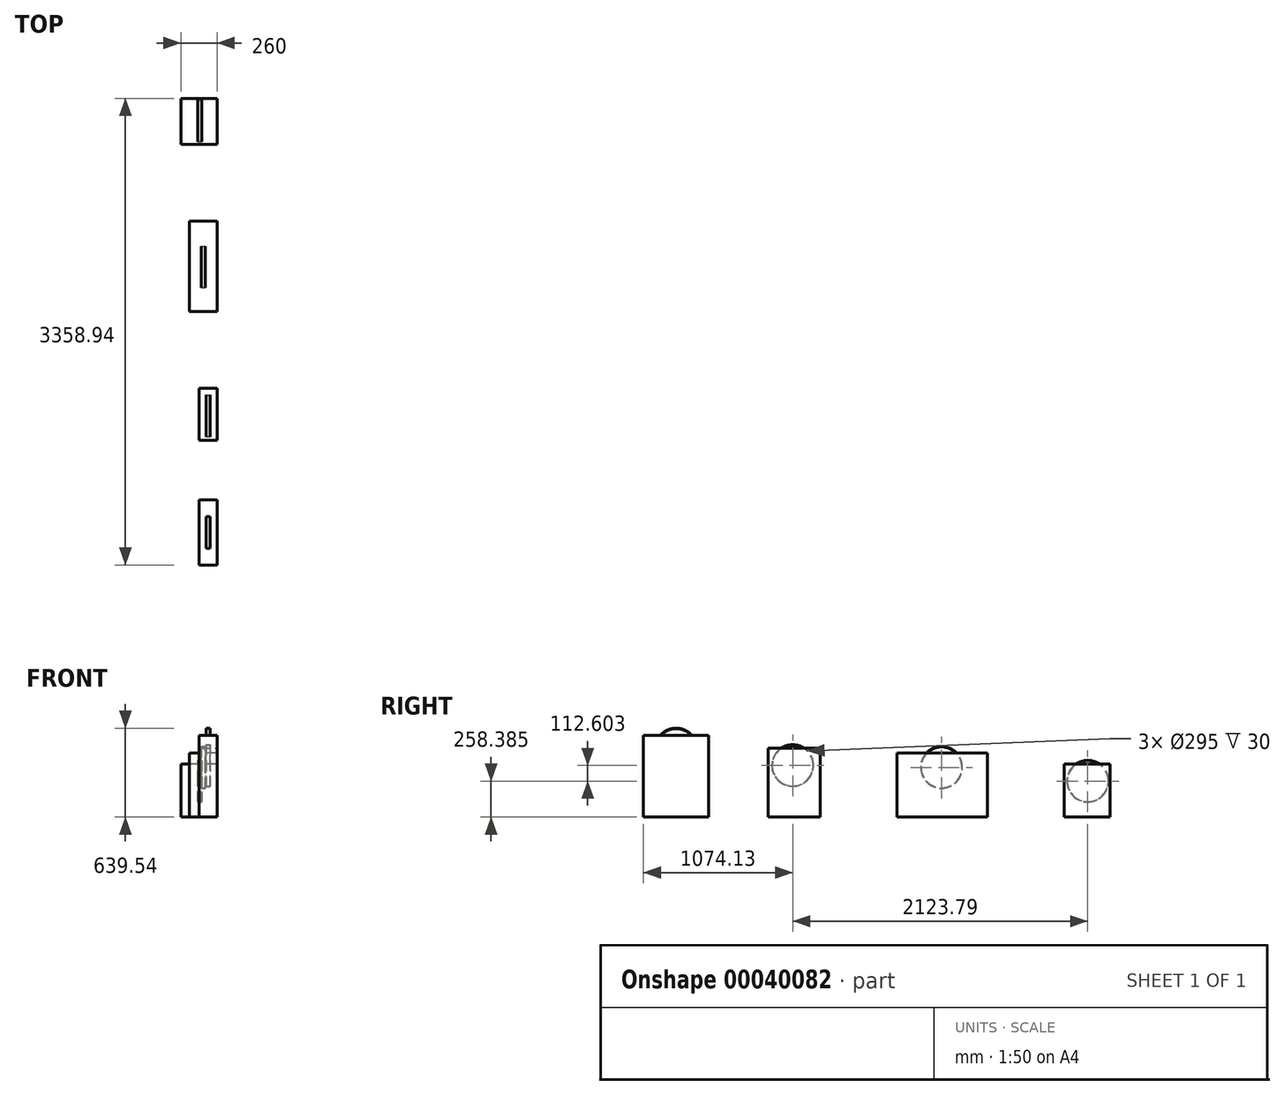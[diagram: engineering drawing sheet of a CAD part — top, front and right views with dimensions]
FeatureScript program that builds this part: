
annotation { "Feature Type Name" : "Feature", "Feature Type Description" : "" }
export const myFeature = defineFeature(function(context is Context, id is Id, definition is map)
    precondition{}
    {
        {
            var Q0;
            Q0=qCreatedBy(makeId("Top.planeOp"),FACE);
            var sketch = newSketch(context, id + "F0", { "sketchPlane" : qUnion([Q0])});
            skLineSegment(sketch, "E0.bottom", {"start": v(-266.62, 237.52) * mm, "end": v(-136.62, 237.52) * mm});
            skLineSegment(sketch, "E0.top", {"start": v(-266.62, -232.48) * mm, "end": v(-136.62, -232.48) * mm});
            skLineSegment(sketch, "E0.left", {"start": v(-266.62, 237.52) * mm, "end": v(-266.62, -232.48) * mm});
            skLineSegment(sketch, "E0.right", {"start": v(-136.62, 237.52) * mm, "end": v(-136.62, -232.48) * mm});
            skLineSegment(sketch, "E1.bottom", {"start": v(-266.62, 664.12) * mm, "end": v(-136.62, 664.12) * mm});
            skLineSegment(sketch, "E1.top", {"start": v(-266.62, 1039.12) * mm, "end": v(-136.62, 1039.12) * mm});
            skLineSegment(sketch, "E1.left", {"start": v(-266.62, 664.12) * mm, "end": v(-266.62, 1039.12) * mm});
            skLineSegment(sketch, "E1.right", {"start": v(-136.62, 664.12) * mm, "end": v(-136.62, 1039.12) * mm});
            skLineSegment(sketch, "E2", {"start": v(-136.62, 237.52) * mm, "end": v(-136.62, 791.19) * mm, "construction": true});
            skLineSegment(sketch, "E3.bottom", {"start": v(-136.62, 1592.79) * mm, "end": v(-336.62, 1592.79) * mm});
            skLineSegment(sketch, "E3.top", {"start": v(-136.62, 2242.79) * mm, "end": v(-336.62, 2242.79) * mm});
            skLineSegment(sketch, "E3.left", {"start": v(-136.62, 1592.79) * mm, "end": v(-136.62, 2242.79) * mm});
            skLineSegment(sketch, "E3.right", {"start": v(-336.62, 1592.79) * mm, "end": v(-336.62, 2242.79) * mm});
            skLineSegment(sketch, "E4.bottom", {"start": v(-136.62, 2796.46) * mm, "end": v(-396.62, 2796.46) * mm});
            skLineSegment(sketch, "E4.top", {"start": v(-136.62, 3126.46) * mm, "end": v(-396.62, 3126.46) * mm});
            skLineSegment(sketch, "E4.left", {"start": v(-136.62, 2796.46) * mm, "end": v(-136.62, 3126.46) * mm});
            skLineSegment(sketch, "E4.right", {"start": v(-396.62, 2796.46) * mm, "end": v(-396.62, 3126.46) * mm});
            skLineSegment(sketch, "E5", {"start": v(-136.62, 1592.79) * mm, "end": v(-136.62, 1039.12) * mm, "construction": true});
            skLineSegment(sketch, "E6", {"start": v(-136.62, 2796.46) * mm, "end": v(-136.62, 2242.79) * mm, "construction": true});
            skSolve(sketch);
        }
        {
            var Q0;
            Q0=makeQuery(id+"F0.imprint","IMPRINT",FACE,{"disambiguationData":[TD([[makeQuery(id+"F0.imprint","IMPRINT",EDGE,{"derivedFrom":sQuery(id+"F0.wireOp",EDGE,"E0.bottom")}),-1.0]])]});
            extrude(context, id + "F1", {"entities" : qUnion([Q0]), "depth" : 587 * mm});
        }
        {
            var Q0;
            Q0=makeQuery(id+"F0.imprint","IMPRINT",FACE,{"disambiguationData":[TD([[makeQuery(id+"F0.imprint","IMPRINT",EDGE,{"derivedFrom":sQuery(id+"F0.wireOp",EDGE,"E1.bottom")}),1.0]])]});
            extrude(context, id + "F2", {"entities" : qUnion([Q0]), "depth" : 495 * mm});
        }
        {
            var Q0;
            Q0=makeQuery(id+"F0.imprint","IMPRINT",FACE,{"disambiguationData":[TD([[makeQuery(id+"F0.imprint","IMPRINT",EDGE,{"derivedFrom":sQuery(id+"F0.wireOp",EDGE,"E3.bottom")}),-1.0]])]});
            extrude(context, id + "F3", {"entities" : qUnion([Q0]), "depth" : 460 * mm});
        }
        {
            var Q0;
            Q0=makeQuery(id+"F0.imprint","IMPRINT",FACE,{"disambiguationData":[TD([[makeQuery(id+"F0.imprint","IMPRINT",EDGE,{"derivedFrom":sQuery(id+"F0.wireOp",EDGE,"E4.bottom")}),-1.0]])]});
            extrude(context, id + "F4", {"entities" : qUnion([Q0]), "depth" : 380 * mm});
        }
        {
            var Q0;
            Q0=makeQuery(id+"F1.opExtrude","SWEPT_FACE",FACE,{"disambiguationData":[OSD([sQuery(id+"F0.wireOp",EDGE,"E0.right")])]});
            var sketch = newSketch(context, id + "F5", { "sketchPlane" : qUnion([Q0])});
            skCircle(sketch, "E7", {"center": v(2.52, 489.54) * mm, "radius": 150 * mm});
            skPoint(sketch, "E8", {"position": v(2.52, 587) * mm});
            skSolve(sketch);
        }
        {
            var Q0;
            Q0 = qSketchRegion(id + "F5", true);
            extrude(context, id + "F6", {"entities" : qUnion([Q0]), "oppositeDirection" : true, "depth" : 30 * mm});
        }
        {
            var Q0;
            Q0=makeQuery(id+"F6.opExtrude","CAP_FACE",FACE,{"disambiguationData":[OSD([sQuery(id+"F5.wireOp",EDGE,"E7")])],"isStart":true});
            var Q1;
            Q1=makeQuery(id+"F6.opExtrude","CAP_FACE",FACE,{"disambiguationData":[OSD([sQuery(id+"F5.wireOp",EDGE,"E7")])],"isStart":false});
            shell(context, id + "F7", {"entities" : qUnion([Q0, Q1]), "thickness" : 2.5 * mm});
        }
        {
            var Q0;
            Q0=makeQuery(id+"F6.opExtrude","SWEPT_BODY",BODY,{"disambiguationData":[OSD([sQuery(id+"F5.wireOp",EDGE,"E7")])]});
            transform(context, id + "F8", {"entities" : qUnion([Q0]), "transformType" : TransformType.TRANSLATION_3D, "dx" : -48.8 * mm, "dy" : 0 * mm, "dz" : 0 * mm, "makeCopy" : false});
        }
        {
            var Q0;
            Q0=makeQuery(id+"F6.opExtrude","SWEPT_BODY",BODY,{"disambiguationData":[OSD([sQuery(id+"F5.wireOp",EDGE,"E7")])]});
            transform(context, id + "F9", {"entities" : qUnion([Q0]), "transformType" : TransformType.TRANSLATION_3D, "dx" : 0 * mm, "dy" : 839.13 * mm, "dz" : -118.56 * mm, "makeCopy" : true});
        }
        {
            var Q0;
            Q0=makeQuery(id+"F9.opPattern","COPY",BODY,{"derivedFrom":makeQuery(id+"F6.opExtrude","SWEPT_BODY",BODY,{"disambiguationData":[OSD([sQuery(id+"F5.wireOp",EDGE,"E7")])]}),"instanceName":"1"});
            transform(context, id + "F10", {"entities" : qUnion([Q0]), "transformType" : TransformType.TRANSLATION_3D, "dx" : -35.22 * mm, "dy" : 1071.27 * mm, "dz" : -13.63 * mm, "makeCopy" : true});
        }
        {
            var Q0;
            Q0=makeQuery(id+"F10.opPattern","COPY",BODY,{"derivedFrom":makeQuery(id+"F9.opPattern","COPY",BODY,{"derivedFrom":makeQuery(id+"F6.opExtrude","SWEPT_BODY",BODY,{"disambiguationData":[OSD([sQuery(id+"F5.wireOp",EDGE,"E7")])]}),"instanceName":"1"}),"instanceName":"1"});
            transform(context, id + "F11", {"entities" : qUnion([Q0]), "transformType" : TransformType.TRANSLATION_3D, "dx" : -26.15 * mm, "dy" : 1052.52 * mm, "dz" : -98.97 * mm, "makeCopy" : true});
        }
        {
            var Q0;
            Q0=makeQuery(id+"F1.opExtrude","SWEPT_BODY",BODY,{"disambiguationData":[OSD([sQuery(id+"F0.wireOp",EDGE,"E0.bottom"),sQuery(id+"F0.wireOp",EDGE,"E0.top"),sQuery(id+"F0.wireOp",EDGE,"E0.left"),sQuery(id+"F0.wireOp",EDGE,"E0.right")])]});
            var Q1;
            Q1=makeQuery(id+"F6.opExtrude","SWEPT_BODY",BODY,{"disambiguationData":[OSD([sQuery(id+"F5.wireOp",EDGE,"E7")])]});
            booleanBodies(context, id + "F12", {"operationType" : BooleanOperationType.SUBTRACTION, "tools" : qUnion([Q0]), "targets" : qUnion([Q1]), "keepTools" : true});
        }
    });
